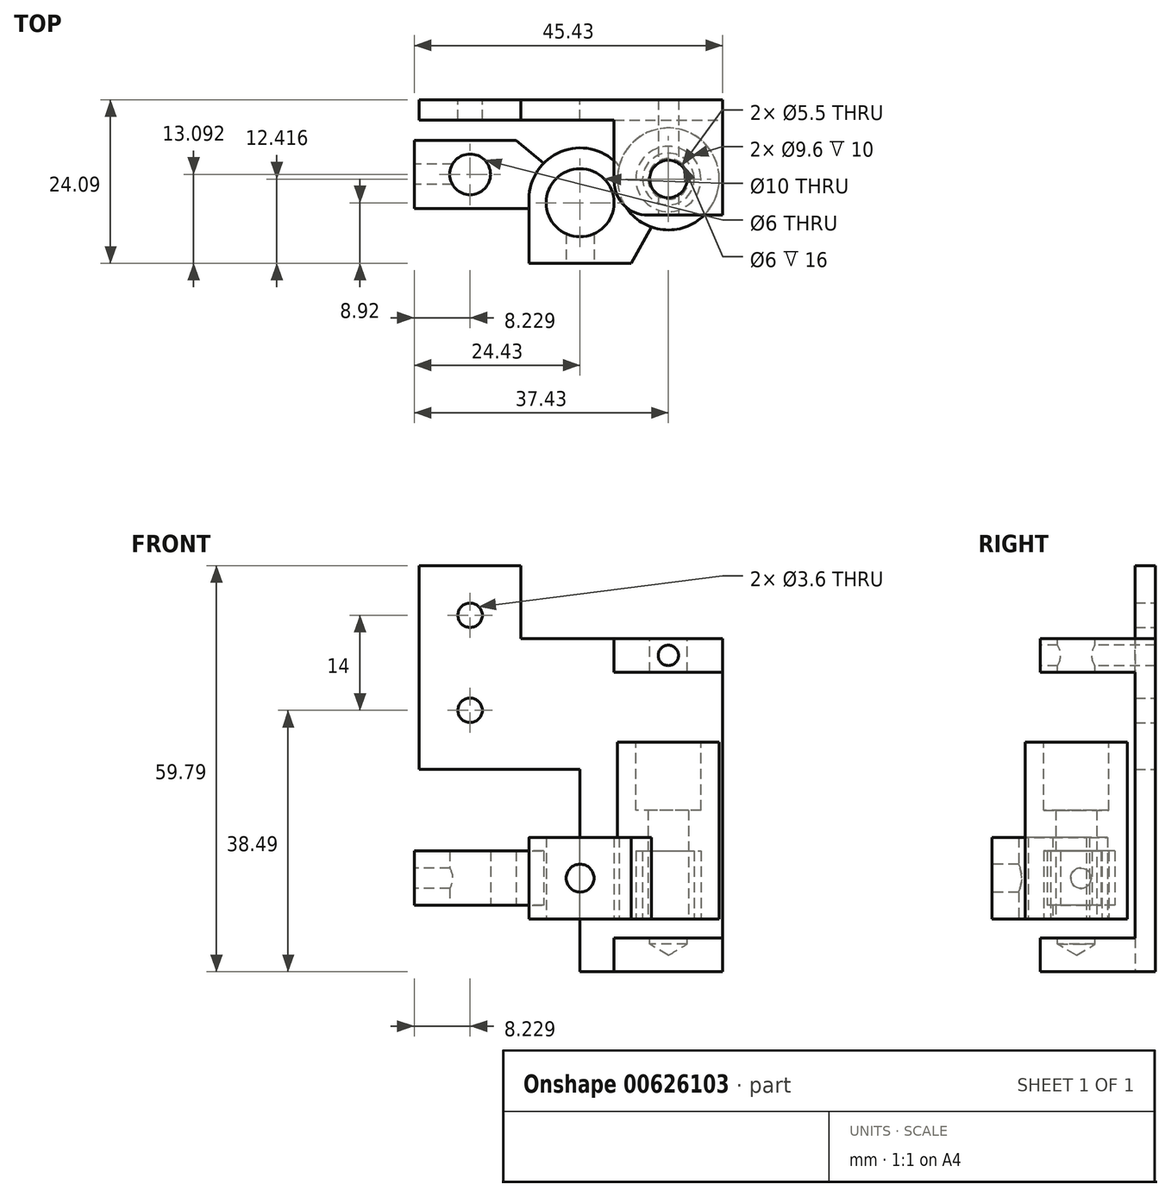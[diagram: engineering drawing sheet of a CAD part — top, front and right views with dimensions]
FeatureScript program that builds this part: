
annotation { "Feature Type Name" : "Feature", "Feature Type Description" : "" }
export const myFeature = defineFeature(function(context is Context, id is Id, definition is map)
    precondition{}
    {
        {
            var Q0;
            Q0=qCreatedBy(makeId("Top.planeOp"),FACE);
            var sketch = newSketch(context, id + "F0", { "sketchPlane" : qUnion([Q0])});
            skCircle(sketch, "E0", {"center": v(-16.2, 4.17) * mm, "radius": 3 * mm});
            skCircle(sketch, "E1", {"center": v(0, 0) * mm, "radius": 5 * mm});
            skCircle(sketch, "E2", {"center": v(13, 3.5) * mm, "radius": 4.8 * mm});
            skLineSegment(sketch, "E3", {"start": v(-26.15, 3.5) * mm, "end": v(35.58, 3.5) * mm, "construction": true});
            skLineSegment(sketch, "E4", {"start": v(-6.47, 0) * mm, "end": v(8.44, 0) * mm, "construction": true});
            skCircle(sketch, "E5", {"center": v(13, 3.5) * mm, "radius": 7.5 * mm});
            skArc(sketch, "E6", {"start": v(7.5, 0) * mm, "mid": v(0, 8.07) * mm, "end": v(-7.5, 0) * mm});
            skLineSegment(sketch, "E7", {"start": v(0, 2.55) * mm, "end": v(0, -2.85) * mm, "construction": true});
            skLineSegment(sketch, "E8", {"start": v(-7.5, 0) * mm, "end": v(-7.5, -8.92) * mm});
            skLineSegment(sketch, "E9", {"start": v(-7.5, -8.92) * mm, "end": v(7.5, -8.92) * mm});
            skLineSegment(sketch, "E10", {"start": v(7.5, -8.92) * mm, "end": v(7.5, 0) * mm});
            skLineSegment(sketch, "E11.bottom", {"start": v(-23.7, 11.67) * mm, "end": v(-8.7, 11.67) * mm, "construction": true});
            skLineSegment(sketch, "E11.top", {"start": v(-23.7, -3.33) * mm, "end": v(-8.7, -3.33) * mm, "construction": true});
            skLineSegment(sketch, "E11.right", {"start": v(-8.7, 11.67) * mm, "end": v(-8.7, -3.33) * mm, "construction": true});
            skLineSegment(sketch, "E12", {"start": v(-20.5, 4.17) * mm, "end": v(-12.54, 4.17) * mm, "construction": true});
            skLineSegment(sketch, "E13", {"start": v(-16.2, 9.11) * mm, "end": v(-16.2, 0) * mm, "construction": true});
            skLineSegment(sketch, "E14", {"start": v(-9.4, 9.17) * mm, "end": v(-24.43, 9.17) * mm});
            skLineSegment(sketch, "E15", {"start": v(-24.43, 9.17) * mm, "end": v(-24.43, -0.83) * mm});
            skLineSegment(sketch, "E16", {"start": v(-24.43, -0.83) * mm, "end": v(-7.5, -0.83) * mm});
            skLineSegment(sketch, "E17", {"start": v(-9.4, 9.17) * mm, "end": v(-5.4, 5.8) * mm});
            skCircle(sketch, "E18", {"center": v(13, 3.5) * mm, "radius": 3 * mm});
            skLineSegment(sketch, "E19", {"start": v(7.5, -8.92) * mm, "end": v(10.52, -3.58) * mm});
            skSolve(sketch);
        }
        {
            var Q0;
            Q0=makeQuery(id+"F0.imprint","IMPRINT",FACE,{"disambiguationData":[TD([[makeQuery(id+"F0.imprint","IMPRINT",EDGE,{"derivedFrom":sQuery(id+"F0.wireOp",EDGE,"E1")}),-1.0]])]});
            var Q1;
            {var subQ0=sQuery(id+"F0.wireOp",EDGE,"E19");Q1=makeQuery(id+"F0.imprint","IMPRINT",FACE,{"disambiguationData":[TD([[makeQuery(id+"F0.imprint","IMPRINT",EDGE,{"derivedFrom":subQ0}),1.0]])]});}
            extrude(context, id + "F1", {"entities" : qUnion([Q0, Q1]), "endBound" : BoundingType.SYMMETRIC, "depth" : 12 * mm, "offsetDistance" : 25 * mm});
        }
        {
            var Q0;
            Q0=makeQuery(id+"F0.imprint","IMPRINT",FACE,{"disambiguationData":[TD([[makeQuery(id+"F0.imprint","IMPRINT",EDGE,{"derivedFrom":sQuery(id+"F0.wireOp",EDGE,"E2")}),-1.0]])]});
            var Q1;
            {var subQ0=sQuery(id+"F0.wireOp",EDGE,"E6");var subQ1=sQuery(id+"F0.wireOp",EDGE,"E5");var subQ2=makeQuery(id+"F0.imprint","INTERSECT",VERTEX,{"derivedFrom":[subQ1,subQ0]});Q1=makeQuery(id+"F0.imprint","IMPRINT",FACE,{"disambiguationData":[TD([[makeQuery(id+"F0.imprint","IMPRINT",EDGE,{"disambiguationData":[TD([[subQ2,-1.0]])],"derivedFrom":subQ1}),1.0]])]});}
            var Q2;
            Q2=makeQuery(id+"F0.imprint","IMPRINT",FACE,{"disambiguationData":[TD([[makeQuery(id+"F0.imprint","IMPRINT",EDGE,{"derivedFrom":sQuery(id+"F0.wireOp",EDGE,"E2")}),1.0]])]});
            extrude(context, id + "F2", {"entities" : qUnion([Q0, Q1, Q2]), "operationType" : NewBodyOperationType.ADD, "depth" : 20 * mm, "offsetDistance" : 25 * mm});
        }
        {
            var Q0;
            {var subQ0=sQuery(id+"F0.wireOp",EDGE,"E6");var subQ1=sQuery(id+"F0.wireOp",EDGE,"E5");var subQ2=makeQuery(id+"F0.imprint","INTERSECT",VERTEX,{"derivedFrom":[subQ1,subQ0]});Q0=makeQuery(id+"F0.imprint","IMPRINT",FACE,{"disambiguationData":[TD([[makeQuery(id+"F0.imprint","IMPRINT",EDGE,{"disambiguationData":[TD([[subQ2,-1.0]])],"derivedFrom":subQ1}),1.0]])]});}
            var Q1;
            Q1=makeQuery(id+"F0.imprint","IMPRINT",FACE,{"disambiguationData":[TD([[makeQuery(id+"F0.imprint","IMPRINT",EDGE,{"derivedFrom":sQuery(id+"F0.wireOp",EDGE,"E2")}),-1.0]])]});
            var Q2;
            Q2=makeQuery(id+"F0.imprint","IMPRINT",FACE,{"disambiguationData":[TD([[makeQuery(id+"F0.imprint","IMPRINT",EDGE,{"derivedFrom":sQuery(id+"F0.wireOp",EDGE,"E2")}),1.0]])]});
            var Q3;
            Q3=makeQuery(id+"F1.opExtrude","CAP_FACE",FACE,{"disambiguationData":[OSD([sQuery(id+"F0.wireOp",EDGE,"E1"),sQuery(id+"F0.wireOp",EDGE,"E5"),sQuery(id+"F0.wireOp",EDGE,"E6"),sQuery(id+"F0.wireOp",EDGE,"E8"),sQuery(id+"F0.wireOp",EDGE,"E9"),sQuery(id+"F0.wireOp",EDGE,"E19")])],"isStart":true});
            extrude(context, id + "F3", {"entities" : qUnion([Q0, Q1, Q2]), "operationType" : NewBodyOperationType.ADD, "endBound" : BoundingType.UP_TO_SURFACE, "oppositeDirection" : true, "depth" : 25 * mm, "endBoundEntityFace" : qUnion([Q3]), "offsetDistance" : 25 * mm});
        }
        {
            var Q0;
            Q0=makeQuery(id+"F0.imprint","IMPRINT",FACE,{"disambiguationData":[TD([[makeQuery(id+"F0.imprint","IMPRINT",EDGE,{"derivedFrom":sQuery(id+"F0.wireOp",EDGE,"E0")}),-1.0]])]});
            extrude(context, id + "F4", {"entities" : qUnion([Q0]), "operationType" : NewBodyOperationType.ADD, "endBound" : BoundingType.SYMMETRIC, "depth" : 8 * mm, "offsetDistance" : 25 * mm});
        }
        {
            var Q0;
            Q0=makeQuery(id+"F2.opExtrude","CAP_FACE",FACE,{"disambiguationData":[OSD([sQuery(id+"F0.wireOp",EDGE,"E5"),sQuery(id+"F0.wireOp",EDGE,"E18")])],"isStart":false});
            var sketch = newSketch(context, id + "F5", { "sketchPlane" : qUnion([Q0])});
            skPoint(sketch, "E20.0", {"position": v(13, 3.5) * mm});
            skCircle(sketch, "E21.0", {"center": v(13, 3.5) * mm, "radius": 4.8 * mm});
            skSolve(sketch);
        }
        {
            var Q0;
            Q0 = qSketchRegion(id + "F5", true);
            extrude(context, id + "F6", {"entities" : qUnion([Q0]), "operationType" : NewBodyOperationType.REMOVE, "oppositeDirection" : true, "depth" : 10 * mm, "offsetDistance" : 25 * mm});
        }
        {
            var Q0;
            {var subQ0=sQuery(id+"F0.wireOp",EDGE,"E5");Q0=makeQuery(id+"F3.boolean.opBoolean","MERGE",FACE,{"derivedFrom":[makeQuery(id+"F1.opExtrude","CAP_FACE",FACE,{"disambiguationData":[OSD([sQuery(id+"F0.wireOp",EDGE,"E1"),subQ0,sQuery(id+"F0.wireOp",EDGE,"E6"),sQuery(id+"F0.wireOp",EDGE,"E8"),sQuery(id+"F0.wireOp",EDGE,"E9"),sQuery(id+"F0.wireOp",EDGE,"E19")])],"isStart":true}),makeQuery(id+"F3.opExtrude","CAP_FACE",FACE,{"disambiguationData":[OSD([subQ0,sQuery(id+"F0.wireOp",EDGE,"E18")])],"isStart":false})]});}
            var sketch = newSketch(context, id + "F7", { "sketchPlane" : qUnion([Q0])});
            skCircle(sketch, "E22.0", {"center": v(13, -3.5) * mm, "radius": 4.8 * mm});
            skCircle(sketch, "E23.0", {"center": v(13, -3.5) * mm, "radius": 3 * mm});
            skCircle(sketch, "E24.0", {"center": v(13, -3.5) * mm, "radius": 3.8 * mm});
            skLineSegment(sketch, "E25.0.0", {"start": v(-7.5, 8.92) * mm, "end": v(-7.5, 0) * mm});
            skArc(sketch, "E25.0.1", {"start": v(-7.5, 0) * mm, "mid": v(-2.84, -7.52) * mm, "end": v(5.75, -5.4) * mm});
            skArc(sketch, "E25.0.2", {"start": v(5.75, -5.4) * mm, "mid": v(19.62, -7.01) * mm, "end": v(10.52, 3.58) * mm});
            skLineSegment(sketch, "E25.0.3", {"start": v(10.52, 3.58) * mm, "end": v(7.5, 8.92) * mm});
            skLineSegment(sketch, "E25.0.4", {"start": v(7.5, 8.92) * mm, "end": v(-7.5, 8.92) * mm});
            skSolve(sketch);
        }
        {
            var Q0;
            Q0=makeQuery(id+"F7.imprint","IMPRINT",FACE,{"disambiguationData":[TD([[makeQuery(id+"F7.imprint","IMPRINT",EDGE,{"derivedFrom":sQuery(id+"F7.wireOp",EDGE,"E24.0")}),-1.0]])]});
            extrude(context, id + "F8", {"entities" : qUnion([Q0]), "operationType" : NewBodyOperationType.REMOVE, "oppositeDirection" : true, "depth" : 10 * mm, "offsetDistance" : 25 * mm});
        }
        {
            var Q0;
            Q0=makeQuery(id+"F4.opExtrude","SWEPT_FACE",FACE,{"disambiguationData":[OSD([sQuery(id+"F0.wireOp",EDGE,"E15")])]});
            var sketch = newSketch(context, id + "F9", { "sketchPlane" : qUnion([Q0])});
            skPoint(sketch, "E26.0", {"position": v(-4.17, 0) * mm});
            skSolve(sketch);
        }
        {
            var Q0;
            Q0=sQuery(id+"F9.wireOp",VERTEX,"E26.0");
            var Q1;
            Q1=makeQuery(id+"F1.opExtrude","SWEPT_BODY",BODY,{"disambiguationData":[OSD([sQuery(id+"F0.wireOp",EDGE,"E1"),sQuery(id+"F0.wireOp",EDGE,"E5"),sQuery(id+"F0.wireOp",EDGE,"E6"),sQuery(id+"F0.wireOp",EDGE,"E8"),sQuery(id+"F0.wireOp",EDGE,"E9"),sQuery(id+"F0.wireOp",EDGE,"E19")])]});
            hole(context, id + "F10", {"style" : HoleStyle.SIMPLE, "endStyle" : HoleEndStyle.BLIND, "holeDiameter" : 3 * mm, "majorDiameter" : 5 * mm, "holeDepth" : 8 * mm, "isTappedThrough" : true, "tappedDepth" : 7 * mm, "tapClearance" : 6, "startFromSketch" : true, "locations" : qUnion([Q0]), "scope" : qUnion([Q1])});
        }
        {
            var Q0;
            Q0=makeQuery(id+"F1.opExtrude","SWEPT_FACE",FACE,{"disambiguationData":[OSD([sQuery(id+"F0.wireOp",EDGE,"E9")])]});
            var sketch = newSketch(context, id + "F11", { "sketchPlane" : qUnion([Q0])});
            skPoint(sketch, "E27.0", {"position": v(0, 0) * mm});
            skSolve(sketch);
        }
        {
            var Q0;
            Q0=sQuery(id+"F11.wireOp",VERTEX,"E27.0");
            var Q1;
            Q1=makeQuery(id+"F1.opExtrude","SWEPT_BODY",BODY,{"disambiguationData":[OSD([sQuery(id+"F0.wireOp",EDGE,"E1"),sQuery(id+"F0.wireOp",EDGE,"E5"),sQuery(id+"F0.wireOp",EDGE,"E6"),sQuery(id+"F0.wireOp",EDGE,"E8"),sQuery(id+"F0.wireOp",EDGE,"E9"),sQuery(id+"F0.wireOp",EDGE,"E19")])]});
            hole(context, id + "F12", {"style" : HoleStyle.SIMPLE, "endStyle" : HoleEndStyle.BLIND, "holeDiameter" : 4.1 * mm, "majorDiameter" : 5 * mm, "holeDepth" : 8 * mm, "isTappedThrough" : true, "tappedDepth" : 7 * mm, "tapClearance" : 6, "startFromSketch" : true, "locations" : qUnion([Q0]), "scope" : qUnion([Q1])});
        }
        {
            var Q0;
            Q0=makeQuery(id+"F4.opExtrude","SWEPT_FACE",FACE,{"disambiguationData":[OSD([sQuery(id+"F0.wireOp",EDGE,"E14")])]});
            cPlane(context, id + "F13", {"entities" : qUnion([Q0]), "cplaneType" : CPlaneType.OFFSET, "offset" : 6 * mm, "width" : 150 * mm, "height" : 150 * mm});
        }
        {
            var Q0;
            Q0=qCreatedBy(id+"F13.planeOp",FACE);
            var sketch = newSketch(context, id + "F14", { "sketchPlane" : qUnion([Q0])});
            skLineSegment(sketch, "E28", {"start": v(23.7, 16) * mm, "end": v(23.7, 46) * mm});
            skLineSegment(sketch, "E29", {"start": v(-21, 35.28) * mm, "end": v(-21, -13.8) * mm});
            skLineSegment(sketch, "E30", {"start": v(-21, -13.8) * mm, "end": v(0, -13.8) * mm});
            skLineSegment(sketch, "E31", {"start": v(0, -13.8) * mm, "end": v(0, 16) * mm});
            skLineSegment(sketch, "E32", {"start": v(0, 16) * mm, "end": v(23.7, 16) * mm});
            skPoint(sketch, "E33.0", {"position": v(-13, 0) * mm});
            skLineSegment(sketch, "E34", {"start": v(-13, 33.32) * mm, "end": v(-13, -35.8) * mm, "construction": true});
            skLineSegment(sketch, "E35.bottom", {"start": v(-5, -8.8) * mm, "end": v(-21, -8.8) * mm});
            skLineSegment(sketch, "E35.top", {"start": v(-5, -13.8) * mm, "end": v(-21, -13.8) * mm});
            skLineSegment(sketch, "E35.left", {"start": v(-5, -8.8) * mm, "end": v(-5, -13.8) * mm});
            skLineSegment(sketch, "E35.right", {"start": v(-21, -8.8) * mm, "end": v(-21, -13.8) * mm});
            skLineSegment(sketch, "E36.bottom", {"start": v(-5, 35.28) * mm, "end": v(-21, 35.28) * mm});
            skLineSegment(sketch, "E36.top", {"start": v(-5, 30.28) * mm, "end": v(-21, 30.28) * mm});
            skLineSegment(sketch, "E36.left", {"start": v(-5, 35.28) * mm, "end": v(-5, 30.28) * mm});
            skLineSegment(sketch, "E36.right", {"start": v(-21, 35.28) * mm, "end": v(-21, 30.28) * mm});
            skPoint(sketch, "E37.0", {"position": v(16.2, 0) * mm});
            skLineSegment(sketch, "E38", {"start": v(16.2, 51.3) * mm, "end": v(16.2, -16.8) * mm, "construction": true});
            skLineSegment(sketch, "E39.0", {"start": v(-20.5, 20) * mm, "end": v(-5.5, 20) * mm});
            skLineSegment(sketch, "E40.0", {"start": v(24.43, 4) * mm, "end": v(7.5, 4) * mm});
            skLineSegment(sketch, "E41", {"start": v(-5, 35.28) * mm, "end": v(8.7, 35.28) * mm});
            skLineSegment(sketch, "E42", {"start": v(8.7, 35.28) * mm, "end": v(8.7, 46) * mm});
            skLineSegment(sketch, "E43", {"start": v(8.7, 46) * mm, "end": v(23.7, 46) * mm});
            skPoint(sketch, "E44", {"position": v(16.2, 38.7) * mm});
            skPoint(sketch, "E45", {"position": v(16.2, 24.7) * mm});
            skSolve(sketch);
        }
        {
            var Q0;
            Q0=makeQuery(id+"F14.imprint","IMPRINT",FACE,{"disambiguationData":[TD([[makeQuery(id+"F14.imprint","IMPRINT",EDGE,{"derivedFrom":sQuery(id+"F14.wireOp",EDGE,"E28")}),1.0]])]});
            extrude(context, id + "F15", {"entities" : qUnion([Q0]), "oppositeDirection" : true, "depth" : 3 * mm, "offsetDistance" : 25 * mm});
        }
        {
            var Q0;
            Q0=makeQuery(id+"F14.imprint","IMPRINT",FACE,{"disambiguationData":[TD([[makeQuery(id+"F14.imprint","IMPRINT",EDGE,{"derivedFrom":sQuery(id+"F14.wireOp",EDGE,"E36.bottom")}),1.0]])]});
            var Q1;
            Q1=makeQuery(id+"F14.imprint","IMPRINT",FACE,{"disambiguationData":[TD([[makeQuery(id+"F14.imprint","IMPRINT",EDGE,{"derivedFrom":sQuery(id+"F14.wireOp",EDGE,"E35.bottom")}),1.0]])]});
            extrude(context, id + "F16", {"entities" : qUnion([Q0, Q1]), "operationType" : NewBodyOperationType.ADD, "oppositeDirection" : true, "depth" : 17 * mm, "offsetDistance" : 25 * mm});
        }
        {
            var Q0;
            Q0=sQuery(id+"F14.wireOp",VERTEX,"E44");
            var Q1;
            Q1=sQuery(id+"F14.wireOp",VERTEX,"E45");
            var Q2;
            Q2=makeQuery(id+"F15.opExtrude","SWEPT_BODY",BODY,{"disambiguationData":[OSD([sQuery(id+"F14.wireOp",EDGE,"E28"),sQuery(id+"F14.wireOp",EDGE,"E29"),sQuery(id+"F14.wireOp",EDGE,"E30"),sQuery(id+"F14.wireOp",EDGE,"E31"),sQuery(id+"F14.wireOp",EDGE,"E32"),sQuery(id+"F14.wireOp",EDGE,"E35.bottom"),sQuery(id+"F14.wireOp",EDGE,"E35.left"),sQuery(id+"F14.wireOp",EDGE,"E36.top"),sQuery(id+"F14.wireOp",EDGE,"E36.left"),sQuery(id+"F14.wireOp",EDGE,"E41"),sQuery(id+"F14.wireOp",EDGE,"E42"),sQuery(id+"F14.wireOp",EDGE,"E43")])]});
            hole(context, id + "F17", {"style" : HoleStyle.SIMPLE, "endStyle" : HoleEndStyle.THROUGH, "holeDiameter" : 3.6 * mm, "majorDiameter" : 5 * mm, "isTappedThrough" : true, "tappedDepth" : 7 * mm, "tapClearance" : 6, "startFromSketch" : true, "locations" : qUnion([Q0, Q1]), "scope" : qUnion([Q2])});
        }
        {
            var Q0;
            {var subQ0=sQuery(id+"F14.wireOp",EDGE,"E36.bottom");var subQ1=sQuery(id+"F14.wireOp",EDGE,"t54O2XWj-5FLe-LaWo-9hj3-ZOWX0ZWZYv9O");Q0=makeQuery(id+"F16.boolean.opBoolean","MERGE",FACE,{"derivedFrom":[makeQuery(id+"F15.opExtrude","SWEPT_FACE",FACE,{"disambiguationData":[OSD([subQ1]),TDD([makeQuery(id+"F14.imprint","IMPRINT",EDGE,{"disambiguationData":[TD([[makeQuery(id+"F14.imprint","INTERSECT",VERTEX,{"derivedFrom":[sQuery(id+"F14.wireOp",EDGE,"E28"),subQ1]}),-1.0]])],"derivedFrom":subQ1})])]}),makeQuery(id+"F15.opExtrude","SWEPT_FACE",FACE,{"disambiguationData":[OSD([subQ1]),TDD([makeQuery(id+"F14.imprint","IMPRINT",EDGE,{"disambiguationData":[TD([[makeQuery(id+"F14.imprint","INTERSECT",VERTEX,{"derivedFrom":[subQ1,sQuery(id+"F14.wireOp",EDGE,"E29")]}),1.0]])],"derivedFrom":subQ1})])]}),makeQuery(id+"F16.opExtrude","SWEPT_FACE",FACE,{"disambiguationData":[OSD([subQ0])]})]});}
            var sketch = newSketch(context, id + "F18", { "sketchPlane" : qUnion([Q0])});
            skPoint(sketch, "E46.0", {"position": v(13, 3.5) * mm});
            skSolve(sketch);
        }
        {
            var Q0;
            Q0=sQuery(id+"F18.wireOp",VERTEX,"E46.0");
            var Q1;
            Q1=makeQuery(id+"F15.opExtrude","SWEPT_BODY",BODY,{"disambiguationData":[OSD([sQuery(id+"F14.wireOp",EDGE,"E28"),sQuery(id+"F14.wireOp",EDGE,"t54O2XWj-5FLe-LaWo-9hj3-ZOWX0ZWZYv9O"),sQuery(id+"F14.wireOp",EDGE,"E29"),sQuery(id+"F14.wireOp",EDGE,"E30"),sQuery(id+"F14.wireOp",EDGE,"E31"),sQuery(id+"F14.wireOp",EDGE,"E32"),sQuery(id+"F14.wireOp",EDGE,"E35.bottom"),sQuery(id+"F14.wireOp",EDGE,"E35.left"),sQuery(id+"F14.wireOp",EDGE,"E35.right"),sQuery(id+"F14.wireOp",EDGE,"E36.top"),sQuery(id+"F14.wireOp",EDGE,"E36.left"),sQuery(id+"F14.wireOp",EDGE,"E36.right")])]});
            hole(context, id + "F19", {"style" : HoleStyle.SIMPLE, "endStyle" : HoleEndStyle.BLIND, "holeDiameter" : 5.5 * mm, "majorDiameter" : 5 * mm, "holeDepth" : 45 * mm, "isTappedThrough" : true, "tappedDepth" : 7 * mm, "tapClearance" : 6, "startFromSketch" : true, "locations" : qUnion([Q0]), "scope" : qUnion([Q1])});
        }
        {
            var Q0;
            Q0=makeQuery(id+"F16.opExtrude","CAP_EDGE",EDGE,{"disambiguationData":[OSD([sQuery(id+"F14.wireOp",EDGE,"E36.left")])],"isStart":false});
            var Q1;
            Q1=makeQuery(id+"F16.opExtrude","CAP_EDGE",EDGE,{"disambiguationData":[OSD([sQuery(id+"F14.wireOp",EDGE,"E36.right")])],"isStart":false});
            var Q2;
            Q2=makeQuery(id+"F16.opExtrude","CAP_EDGE",EDGE,{"disambiguationData":[OSD([sQuery(id+"F14.wireOp",EDGE,"E35.left")])],"isStart":false});
            var Q3;
            Q3=makeQuery(id+"F16.opExtrude","CAP_EDGE",EDGE,{"disambiguationData":[OSD([sQuery(id+"F14.wireOp",EDGE,"E35.right")])],"isStart":false});
            fillet(context, id + "F20", {"entities" : qUnion([Q0, Q1, Q2, Q3]), "radius" : 5 * mm, "tangentPropagation" : true, "allowEdgeOverflow" : false});
        }
        {
            var Q0;
            Q0=makeQuery(id+"F16.opExtrude","CAP_FACE",FACE,{"disambiguationData":[OSD([sQuery(id+"F14.wireOp",EDGE,"E36.bottom"),sQuery(id+"F14.wireOp",EDGE,"E36.top"),sQuery(id+"F14.wireOp",EDGE,"E36.left"),sQuery(id+"F14.wireOp",EDGE,"E36.right")])],"isStart":false});
            var sketch = newSketch(context, id + "F21", { "sketchPlane" : qUnion([Q0])});
            skLineSegment(sketch, "E47.1", {"start": v(5, 35.28) * mm, "end": v(21, 35.28) * mm});
            skLineSegment(sketch, "E47.2", {"start": v(10, 35.28) * mm, "end": v(16, 35.28) * mm});
            skLineSegment(sketch, "E47.3", {"start": v(10, 30.28) * mm, "end": v(16, 30.28) * mm});
            skPoint(sketch, "E48", {"position": v(13, 35.28) * mm});
            skPoint(sketch, "E49.0", {"position": v(10, 32.78) * mm});
            skPoint(sketch, "E50", {"position": v(13, 32.78) * mm});
            skPoint(sketch, "E51.0", {"position": v(10, -11.3) * mm});
            skPoint(sketch, "E52.0", {"position": v(13, -8.8) * mm});
            skPoint(sketch, "E53", {"position": v(13, -11.3) * mm});
            skSolve(sketch);
        }
        {
            var Q0;
            Q0=sQuery(id+"F21.wireOp",VERTEX,"E50");
            var Q1;
            Q1=makeQuery(id+"F15.opExtrude","SWEPT_BODY",BODY,{"disambiguationData":[OSD([sQuery(id+"F14.wireOp",EDGE,"E28"),sQuery(id+"F14.wireOp",EDGE,"E29"),sQuery(id+"F14.wireOp",EDGE,"E30"),sQuery(id+"F14.wireOp",EDGE,"E31"),sQuery(id+"F14.wireOp",EDGE,"E32"),sQuery(id+"F14.wireOp",EDGE,"E35.bottom"),sQuery(id+"F14.wireOp",EDGE,"E35.left"),sQuery(id+"F14.wireOp",EDGE,"E36.top"),sQuery(id+"F14.wireOp",EDGE,"E36.left"),sQuery(id+"F14.wireOp",EDGE,"E41"),sQuery(id+"F14.wireOp",EDGE,"E42"),sQuery(id+"F14.wireOp",EDGE,"E43")])]});
            hole(context, id + "F22", {"style" : HoleStyle.SIMPLE, "endStyle" : HoleEndStyle.THROUGH, "holeDiameter" : 3 * mm, "majorDiameter" : 5 * mm, "isTappedThrough" : true, "tappedDepth" : 7 * mm, "tapClearance" : 6, "startFromSketch" : true, "locations" : qUnion([Q0]), "scope" : qUnion([Q1])});
        }
    });
